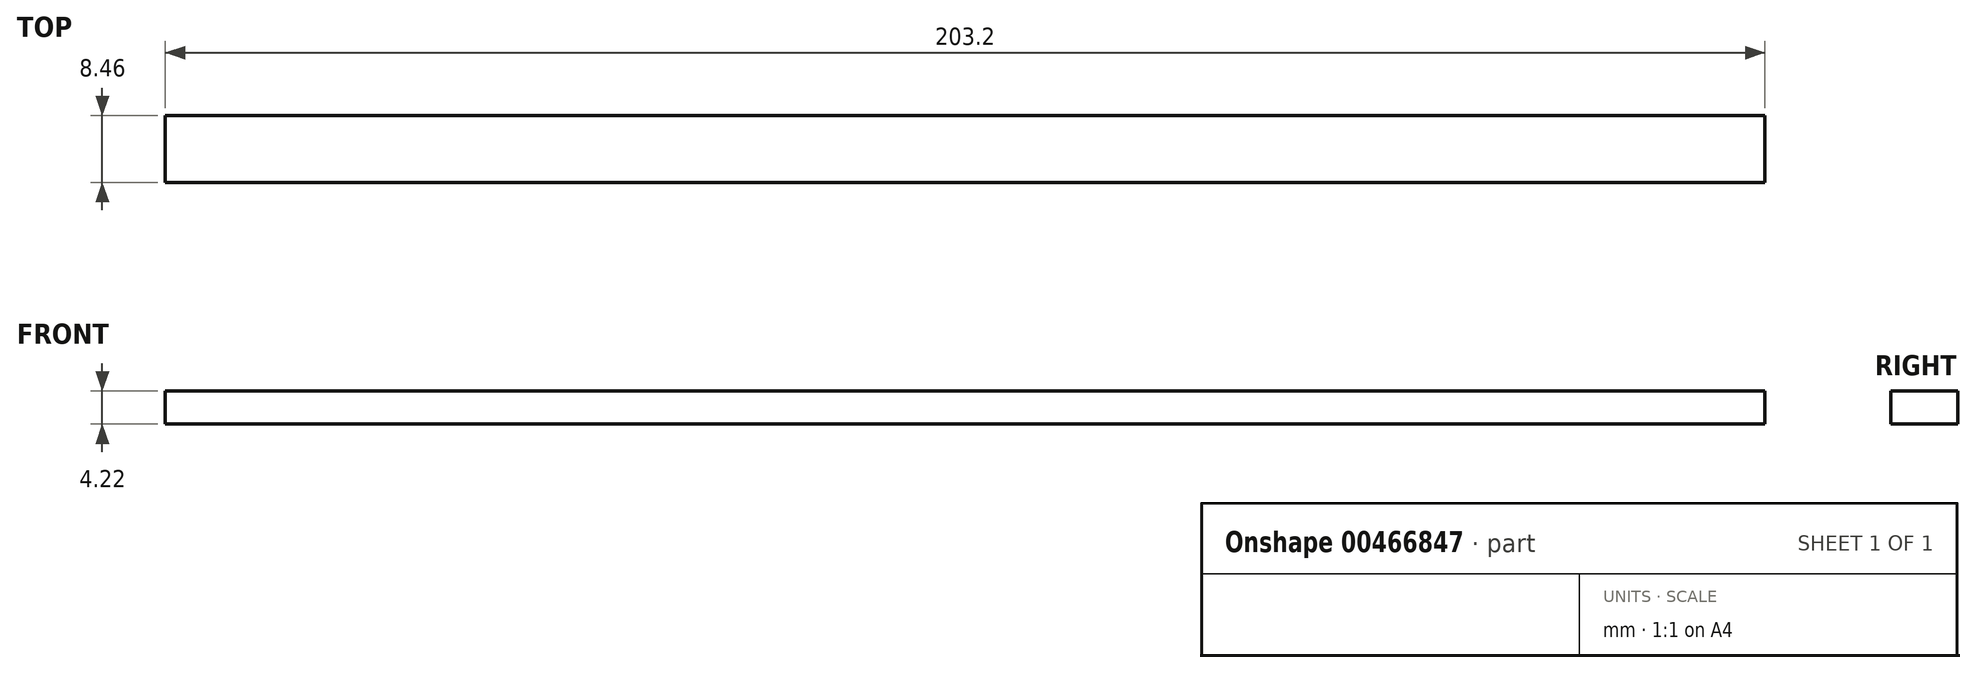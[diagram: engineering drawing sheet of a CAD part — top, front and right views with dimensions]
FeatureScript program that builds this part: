
annotation { "Feature Type Name" : "Feature", "Feature Type Description" : "" }
export const myFeature = defineFeature(function(context is Context, id is Id, definition is map)
    precondition{}
    {
        {
            var Q0;
            Q0=qCreatedBy(makeId("Top.planeOp"),FACE);
            var sketch = newSketch(context, id + "F0", { "sketchPlane" : qUnion([Q0])});
            skLineSegment(sketch, "E0.bottom", {"start": v(-41.76, 22.28) * mm, "end": v(161.44, 22.28) * mm});
            skLineSegment(sketch, "E0.top", {"start": v(-41.76, 13.82) * mm, "end": v(161.44, 13.82) * mm});
            skLineSegment(sketch, "E0.left", {"start": v(-41.76, 22.28) * mm, "end": v(-41.76, 13.82) * mm});
            skLineSegment(sketch, "E0.right", {"start": v(161.44, 22.28) * mm, "end": v(161.44, 13.82) * mm});
            skSolve(sketch);
        }
        {
            var Q0;
            Q0=makeQuery(id+"F0.imprint","IMPRINT",FACE,{"disambiguationData":[TD([[makeQuery(id+"F0.imprint","IMPRINT",EDGE,{"derivedFrom":sQuery(id+"F0.wireOp",EDGE,"E0.bottom")}),-1.0]])]});
            extrude(context, id + "F1", {"entities" : qUnion([Q0]), "depth" : 4.22 * mm});
        }
    });
